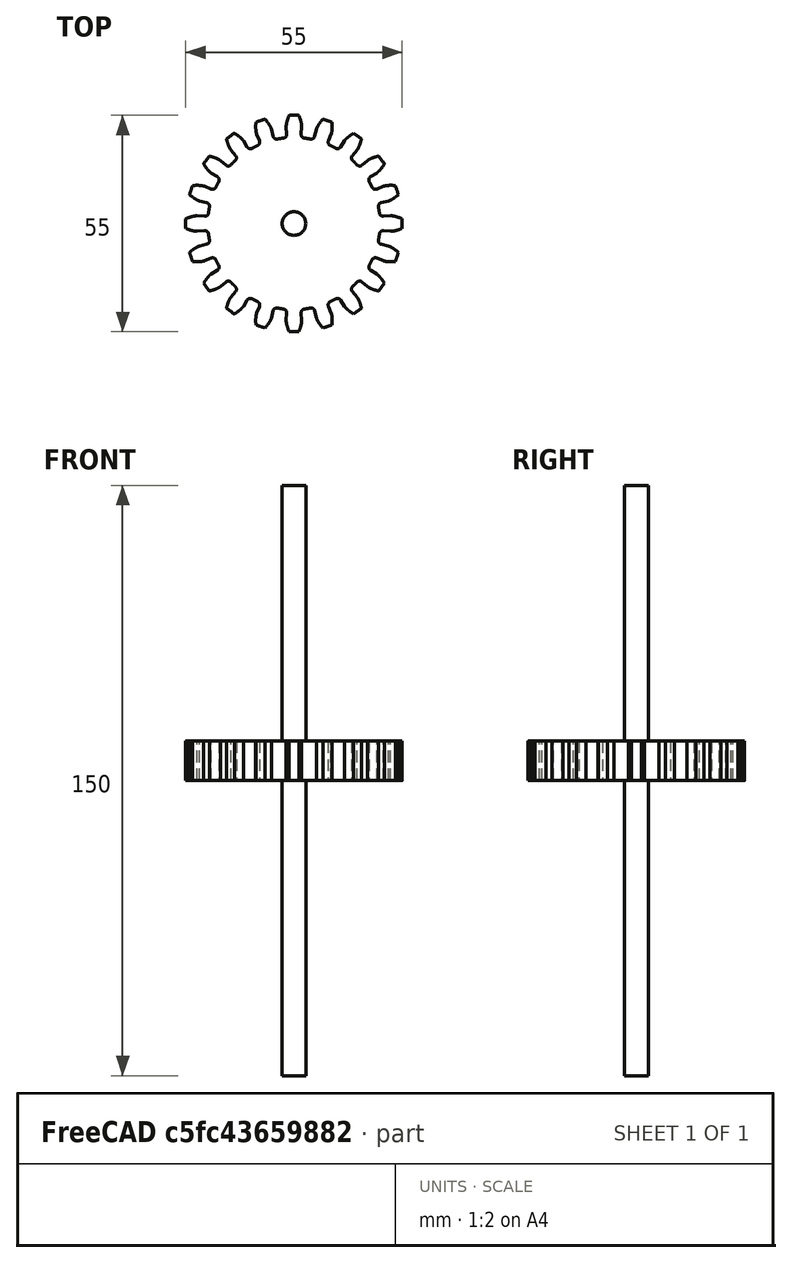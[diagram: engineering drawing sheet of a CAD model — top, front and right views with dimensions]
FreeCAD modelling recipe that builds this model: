
FCSTD DOCUMENT  (FreeCAD 0.16R6705 (Git))
Label: ingranaggio
License: All rights reserved
LicenseURL: http://it.wikipedia.org/wiki/<copyright redacted>
objects: PartDesign::Pad×2, Part::Part2DObjectPython×1, Sketcher::SketchObject×1, Part::MultiFuse×1, App::MeasureDistance×1
note: 7 computed .brp shape members not serialized (recipe doc carries the construction recipe); baked Part::Feature solids carry a one-line shape summary decoded from their .brp

FEATURE [Part::Part2DObjectPython] InvoluteGear  # Draft 2D object (typed FeaturePython)
  ExternalGear = true
  HighPrecision = true
  Modules = 2.5
  NumberOfTeeth = 20
  PressureAngle = 10
FEATURE [PartDesign::Pad] Pad
  Length = 10
  Length2 = 100
  Sketch = -> InvoluteGear
  Type = 0
FEATURE [Sketcher::SketchObject] Sketch001
  Placement = pos=(0,0,0) rot=(1,0,0;3.14159rad)
  sketch-geometry (1):
    g0: Circle CenterX=0 CenterY=0 CenterZ=0 NormalX=0 NormalY=0 NormalZ=1 Radius=3.00999
FEATURE [PartDesign::Pad] Pad002
  Length = 150
  Length2 = 200
  Midplane = true
  Placement = pos=(0,0,0) rot=(1,0,0;3.14159rad)
  Sketch = -> Sketch001
  Type = 0
FEATURE [Part::MultiFuse] Fusion
  Shapes = -> [Pad002,Pad]
FEATURE [App::MeasureDistance] Distance  label="Distance: 150 mm"
  Distance = 150
  P1 = (0.188999,-3.00405,75)
  P2 = (0.188999,-3.00405,-75)
